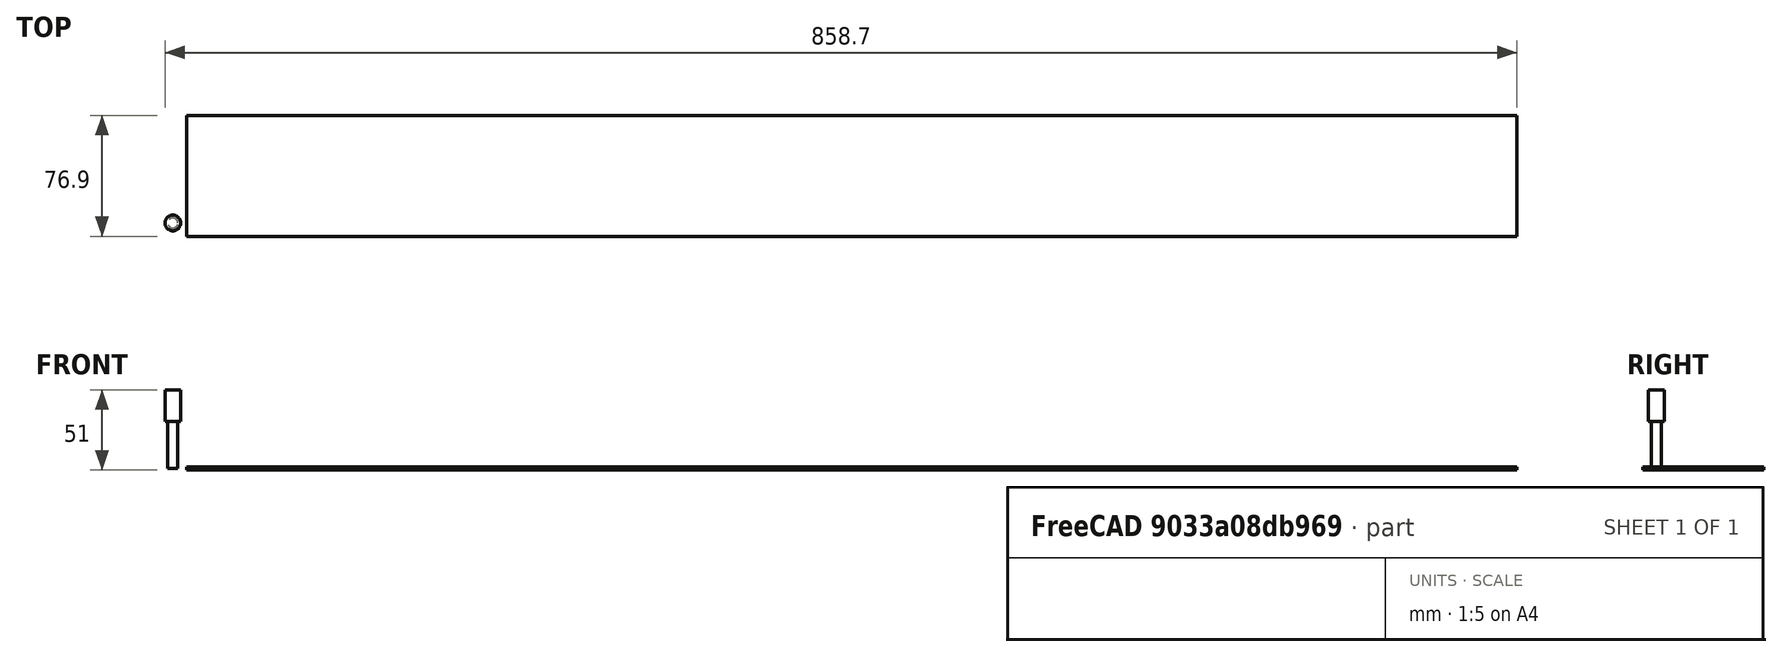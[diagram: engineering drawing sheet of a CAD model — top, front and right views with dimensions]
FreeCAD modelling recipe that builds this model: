
FCSTD DOCUMENT  (FreeCAD 0.19R14555 (Git shallow))
Label: MSSignBig
License: All rights reserved
LicenseURL: http://en.wikipedia.org/wiki/All_rights_reserved
objects: Path::FeaturePython×3, Part::Part2DObjectPython×2, App::DocumentObjectGroup×2, Part::FeaturePython×2, PartDesign::Body×1, App::FeaturePython×1, Path::FeatureCompoundPython×1
note: 5 computed .brp shape members not serialized (recipe doc carries the construction recipe); baked Part::Feature solids carry a one-line shape summary decoded from their .brp

FEATURE [PartDesign::Body] Body
  Origin = -> Origin
FEATURE [Part::Part2DObjectPython] ShapeString  # Draft 2D object (typed FeaturePython)
  FontFile = <userpath>/Documents/MensShed/FreeCAD/CamBam Stick Fonts/1CamBam_Stick_5.ttf
  Size = 32
  String = The Men's Shed
  Tracking = 0
FEATURE [App::FeaturePython] SetupSheet  # Path/CAM operation (typed FeaturePython)
  ClearanceHeightExpression = OpStockZMax+SetupSheet.ClearanceHeightOffset
  ClearanceHeightOffset = 5
  CoolantMode = 0
  CoolantModes = None | Flood | Mist
  FinalDepthExpression = OpFinalDepth
  HorizRapid = 0
  SafeHeightExpression = OpStockZMax+SetupSheet.SafeHeightOffset
  SafeHeightOffset = 3
  StartDepthExpression = OpStartDepth
  StepDownExpression = OpToolDiameter
  VertRapid = 0
FEATURE [Part::Part2DObjectPython] Clone2D  label="Model-ShapeString"  # Draft 2D object (typed FeaturePython)
  Fuse = false
  Objects = -> [ShapeString]
  PathResource = Model
  Scale = (1,1,1)
FEATURE [App::DocumentObjectGroup] Model
  Group = -> [Clone2D]
FEATURE [Part::FeaturePython] Stock  # WARN: FeaturePython — macro-defined, semantics opaque (R4)
  Base = -> Model
  ExtXneg = 1
  ExtXpos = 1
  ExtYneg = 1
  ExtYpos = 1
  ExtZneg = 1
  ExtZpos = 1
  Placement = pos=(9.74679,-7.5156,0) rot=(0,0,1;0rad)
  StockType = FromBase
FEATURE [Part::FeaturePython] ToolBit001  label="6.4mm Endmill"  # Path/CAM toolbit (typed FeaturePython)
  BitPropertyNames = Chipload | CuttingEdgeHeight | Diameter | Flutes | Length | Material | ShankDiameter
  BitShape = /app/freecad/Mod/Path/Tools/Shape/endmill.fcstd
  Chipload = 0
  CuttingEdgeHeight = 30
  Diameter = 6.4
  File = <userpath>/Documents/MensShed/FreeCAD/Bit/6.4mm_Endmill.fctb
  Flutes = 0
  Length = 50
  Material = 0
  ShankDiameter = 10
  ShapeName = endmill
FEATURE [Path::FeaturePython] __4mm_Endmill  label="6.4mm Endmill001"  # Path/CAM operation (typed FeaturePython)
  HorizFeed = 10
  HorizRapid = 0
  SpindleDir = 0
  SpindleSpeed = 10000
  Tool = -> ToolBit001
  ToolNumber = 1
  VertFeed = 10
  VertRapid = 0
  expr: VertRapid = SetupSheet.VertRapid
  expr: HorizRapid = SetupSheet.HorizRapid
FEATURE [App::DocumentObjectGroup] Tools
  Group = -> [__4mm_Endmill]
FEATURE [Path::FeaturePython] Engrave  # Path/CAM operation (typed FeaturePython)
  Active = true
  ClearanceHeight = 6
  CoolantMode = None
  CycleTime = 00:14:07
  FinalDepth = -3
  OpFinalDepth = -1.5
  OpStartDepth = 0
  OpStockZMax = 1
  OpStockZMin = -1
  OpToolDiameter = 6.4
  SafeHeight = 4
  StartDepth = 0
  StartVertex = 0
  StepDown = 1.5
  ToolController = -> __4mm_Endmill
  expr: StartDepth = 0
  expr: FinalDepth = -3
  expr: StepDown = 1.5mm
  expr: SafeHeight = OpStockZMax + SetupSheet.SafeHeightOffset
  expr: ClearanceHeight = OpStockZMax + SetupSheet.ClearanceHeightOffset
FEATURE [Path::FeatureCompoundPython] Operations  # Path/CAM operation (typed FeaturePython)
  Group = -> [Engrave]
  UsePlacements = false
FEATURE [Path::FeaturePython] Job  # Path/CAM operation (typed FeaturePython)
  CycleTime = 00:14:07
  Fixtures = G54
  GeometryTolerance = 0.01
  LastPostProcessDate = 2021-12-07 09:43:57.742759
  LastPostProcessOutput = <userpath>/Documents/MensShed/MSSignBig.ngc
  Model = -> Model
  Operations = -> Operations
  OrderOutputBy = 0
  PostProcessor = 7
  PostProcessorOutputFile = <userpath>/Documents/MensShed/MSSignBig.ngc
  SetupSheet = -> SetupSheet
  SplitOutput = false
  Stock = -> Stock
  Tools = -> Tools
